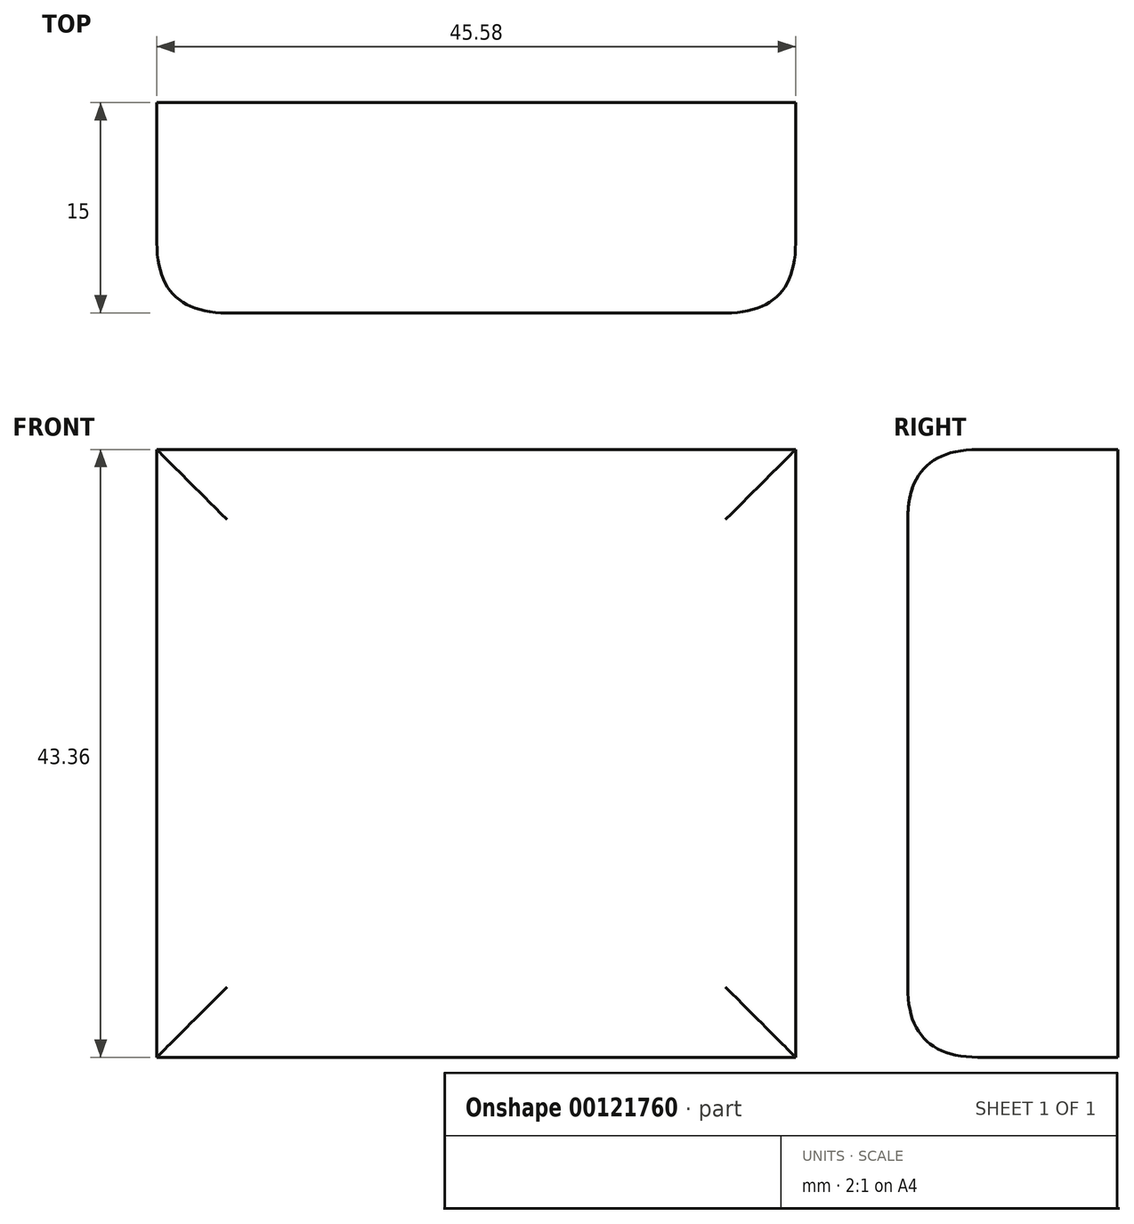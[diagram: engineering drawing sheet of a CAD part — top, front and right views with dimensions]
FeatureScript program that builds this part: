
annotation { "Feature Type Name" : "Feature", "Feature Type Description" : "" }
export const myFeature = defineFeature(function(context is Context, id is Id, definition is map)
    precondition{}
    {
        {
            var Q0;
            Q0=qCreatedBy(makeId("Front.planeOp"),FACE);
            var sketch = newSketch(context, id + "F0", { "sketchPlane" : qUnion([Q0])});
            skLineSegment(sketch, "E0.bottom", {"start": v(22.79, -21.68) * mm, "end": v(-22.79, -21.68) * mm});
            skLineSegment(sketch, "E0.top", {"start": v(22.79, 21.68) * mm, "end": v(-22.79, 21.68) * mm});
            skLineSegment(sketch, "E0.left", {"start": v(22.79, -21.68) * mm, "end": v(22.79, 21.68) * mm});
            skLineSegment(sketch, "E0.right", {"start": v(-22.79, -21.68) * mm, "end": v(-22.79, 21.68) * mm});
            skPoint(sketch, "E0.middle", {"position": v(0, 0) * mm});
            skSolve(sketch);
        }
        {
            var Q0;
            Q0=makeQuery(id+"F0.imprint","IMPRINT",FACE,{"disambiguationData":[TD([[makeQuery(id+"F0.imprint","IMPRINT",EDGE,{"derivedFrom":sQuery(id+"F0.wireOp",EDGE,"E0.bottom")}),-1.0]])]});
            extrude(context, id + "F1", {"entities" : qUnion([Q0]), "depth" : 15 * mm});
        }
        {
            var Q0;
            Q0=makeQuery(id+"F1.opExtrude","CAP_EDGE",EDGE,{"disambiguationData":[OSD([sQuery(id+"F0.wireOp",EDGE,"E0.top")])],"isStart":false});
            var Q1;
            Q1=makeQuery(id+"F1.opExtrude","CAP_EDGE",EDGE,{"disambiguationData":[OSD([sQuery(id+"F0.wireOp",EDGE,"E0.left")])],"isStart":false});
            var Q2;
            Q2=makeQuery(id+"F1.opExtrude","CAP_EDGE",EDGE,{"disambiguationData":[OSD([sQuery(id+"F0.wireOp",EDGE,"E0.bottom")])],"isStart":false});
            var Q3;
            Q3=makeQuery(id+"F1.opExtrude","CAP_EDGE",EDGE,{"disambiguationData":[OSD([sQuery(id+"F0.wireOp",EDGE,"E0.right")])],"isStart":false});
            fillet(context, id + "F2", {"entities" : qUnion([Q0, Q1, Q2, Q3]), "radius" : 5 * mm, "rho" : 0.5, "crossSection" : FilletCrossSection.CONIC, "allowEdgeOverflow" : false});
        }
    });
